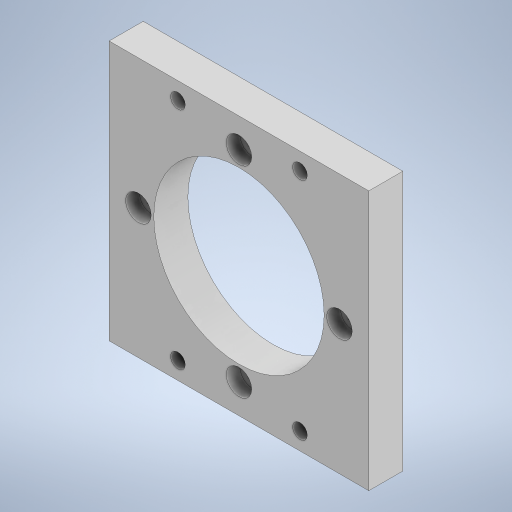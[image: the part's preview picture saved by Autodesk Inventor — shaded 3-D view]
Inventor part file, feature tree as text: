
AUTODESK INVENTOR PART (.ipt)
format: ipt  version: 2023 (Build 270158000, 158)  size: 267,264 bytes
history: native  units: mm
features: sketch x3, hole x2, projected_geometry x1, extrude x1
ambient origin geometry x8: Origin, YZ Plane, XZ Plane, XY Plane, X Axis, Y Axis, Z Axis, Center Point
bodies: Solid1 (feature_tree)
feature tree (7):
  hole  "Hole1"  [1 undecoded]
  hole  "Hole2"  [1 undecoded]
  sketch  "Sketch3"  dims[d7=4.1mm d8=8.0mm d9=7.5mm d10=4.0mm d11=90.0deg d12=8.0mm d13=20.594885mm d14=17.9085mm]
  sketch  "Sketch4"  dims[d15=33.02mm d16=4.318mm d17=6.0mm d18=7.2mm d19=4.4mm d20=90.0deg d21=8.0mm d22=20.594885mm]
  projected_geometry  "Projected Loop1"
  sketch  "Sketch2"  dims[d0=50.0mm d1=76.2mm d2=76.2mm d4=0.0mm d5=10.0mm d6=59.0mm]
  extrude  "Extrusion1"  [1 undecoded]
note: 3 required parameter values undecoded (feature->parameter linkage not recoverable at this tier; creation-order binding heuristic only, values carry confidence <= 0.55)
